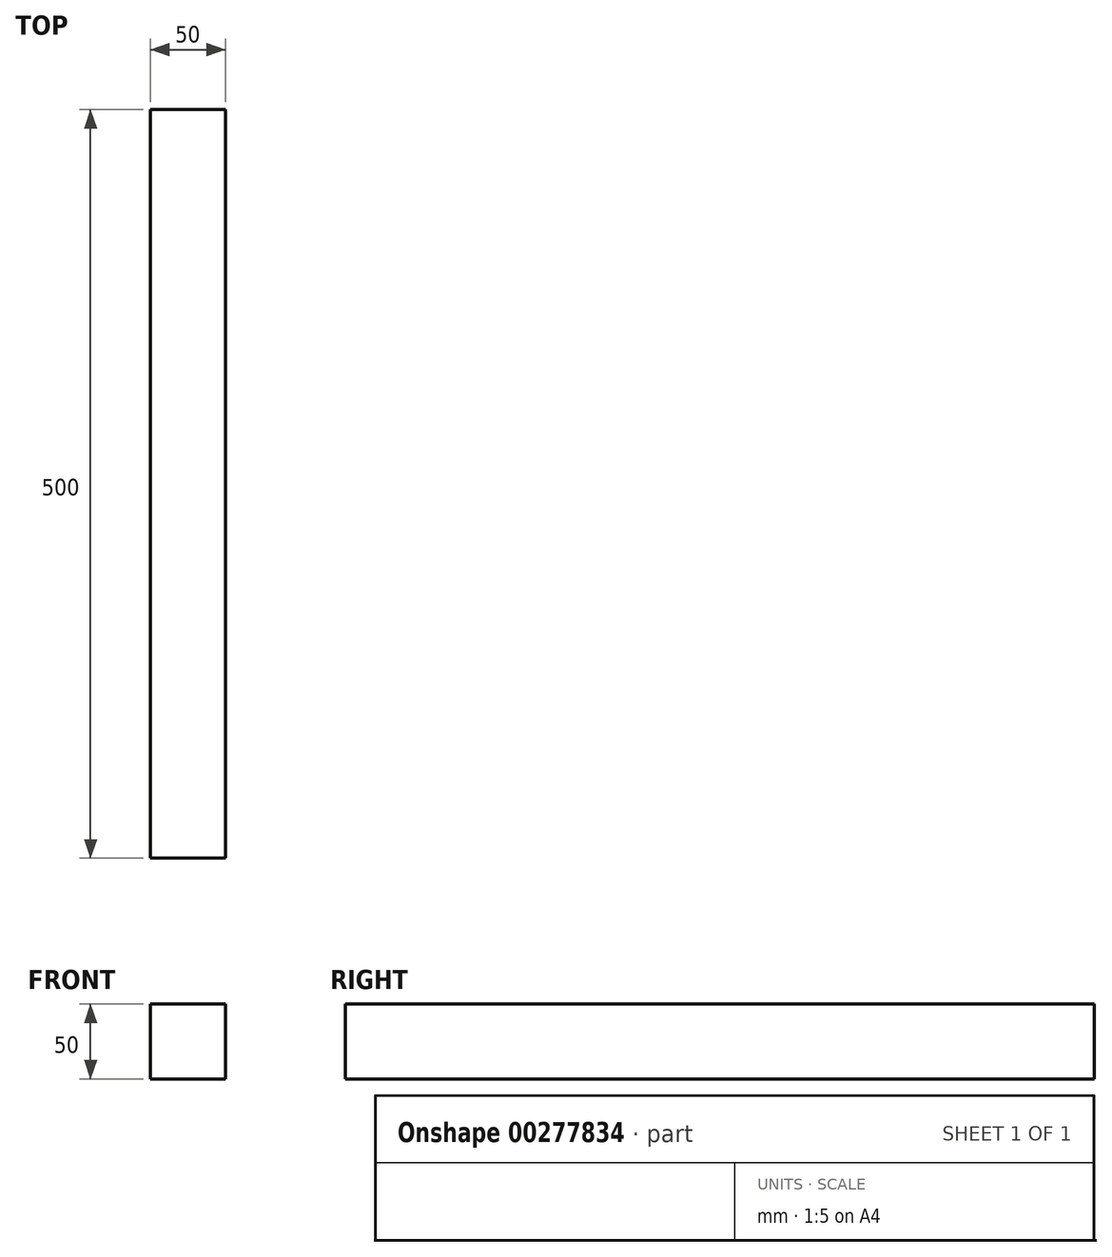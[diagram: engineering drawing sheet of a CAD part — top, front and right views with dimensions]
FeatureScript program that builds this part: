
annotation { "Feature Type Name" : "Feature", "Feature Type Description" : "" }
export const myFeature = defineFeature(function(context is Context, id is Id, definition is map)
    precondition{}
    {
        {
            var Q0;
            Q0=qCreatedBy(makeId("Front.planeOp"),FACE);
            var sketch = newSketch(context, id + "F0", { "sketchPlane" : qUnion([Q0])});
            skLineSegment(sketch, "E0.bottom", {"start": v(25, -25) * mm, "end": v(-25, -25) * mm});
            skLineSegment(sketch, "E0.top", {"start": v(25, 25) * mm, "end": v(-25, 25) * mm});
            skLineSegment(sketch, "E0.left", {"start": v(25, -25) * mm, "end": v(25, 25) * mm});
            skLineSegment(sketch, "E0.right", {"start": v(-25, -25) * mm, "end": v(-25, 25) * mm});
            skPoint(sketch, "E0.middle", {"position": v(0, 0) * mm});
            skSolve(sketch);
        }
        {
            var Q0;
            Q0=makeQuery(id+"F0.imprint","IMPRINT",FACE,{"disambiguationData":[TD([[makeQuery(id+"F0.imprint","IMPRINT",EDGE,{"derivedFrom":sQuery(id+"F0.wireOp",EDGE,"E0.bottom")}),-1.0]])]});
            extrude(context, id + "F1", {"entities" : qUnion([Q0]), "oppositeDirection" : true, "depth" : 500 * mm});
        }
    });
